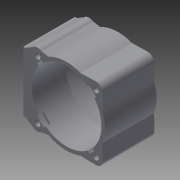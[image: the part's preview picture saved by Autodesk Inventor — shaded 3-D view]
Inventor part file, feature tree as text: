
AUTODESK INVENTOR PART (.ipt)
format: ipt  version: 2014 SP2 (Build 180246200, 246)  size: 231,424 bytes
history: native  units: mm
features: extrude x3, sketch x3, chamfer x1
ambient origin geometry x8: Origin, YZ Plane, XZ Plane, XY Plane, X Axis, Y Axis, Z Axis, Center Point
bodies: Solid1 (feature_tree)
feature tree (7):
  extrude  "Extrusion1"  Depth=4.0mm
  extrude  "Extrusion2"  Depth=39.0mm
  chamfer  "Chamfer1"  Distance=5.0mm
  extrude  "Extrusion3"  Depth=4.0mm
  sketch  "Sketch2"  dims[d0=4.0mm d1=0.0mm d9=58.0mm]
  sketch  "Sketch4"  dims[d10=39.0mm d11=0.0mm d12=5.0mm]
  sketch  "Sketch5"  dims[d13=5.0mm d14=5.0mm d15=5.0mm d16=5.0mm d17=5.0mm d18=10.5mm d19=2.0mm d20=45.0deg d21=65.0mm d22=65.0mm d23=32.0mm d24=32.0mm d25=62.0mm d26=54.0mm d27=4.0mm d28=4.0mm d29=4.0mm d30=4.0mm d31=4.0mm d32=4.0mm d33=4.0mm d34=4.0mm d35=4.0mm d36=0.0mm]
